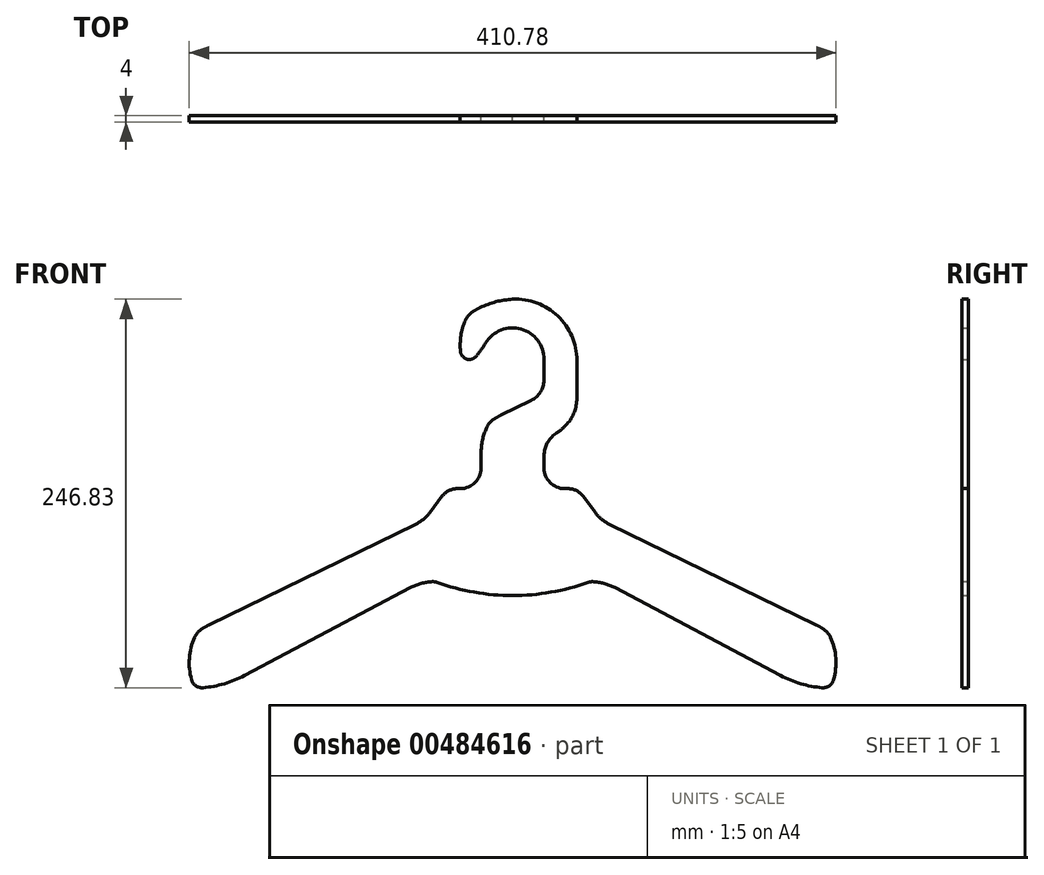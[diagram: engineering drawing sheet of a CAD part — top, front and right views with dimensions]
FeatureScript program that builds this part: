
annotation { "Feature Type Name" : "Feature", "Feature Type Description" : "" }
export const myFeature = defineFeature(function(context is Context, id is Id, definition is map)
    precondition{}
    {
        {
            var Q0;
            Q0=qCreatedBy(makeId("Front.planeOp"),FACE);
            var sketch = newSketch(context, id + "F0", { "sketchPlane" : qUnion([Q0])});
            skLineSegment(sketch, "E0", {"start": v(0, 0) * mm, "end": v(0, 266.9) * mm, "construction": true});
            skLineSegment(sketch, "E1", {"start": v(0, 0) * mm, "end": v(0, -107.96) * mm, "construction": true});
            skSolve(sketch);
        }
        {
            var Q0;
            Q0=qCreatedBy(makeId("Front.planeOp"),FACE);
            var sketch = newSketch(context, id + "F1", { "sketchPlane" : qUnion([Q0])});
            skLineSegment(sketch, "E2", {"start": v(-52.5, 94.84) * mm, "end": v(-44.73, 105.2) * mm});
            skLineSegment(sketch, "E3", {"start": v(-35.13, 110) * mm, "end": v(0, 110) * mm});
            skPoint(sketch, "E4.visualSharp", {"position": v(-56.13, 90) * mm});
            skArc(sketch, "E4.filletArc", {"start": v(-61.56, 87.36) * mm, "mid": v(-56.58, 90.56) * mm, "end": v(-52.5, 94.84) * mm});
            skPoint(sketch, "E5.visualSharp", {"position": v(-41.13, 110) * mm});
            skArc(sketch, "E5.filletArc", {"start": v(-35.13, 110) * mm, "mid": v(-40.5, 108.73) * mm, "end": v(-44.73, 105.2) * mm});
            skLineSegment(sketch, "E6.trimOffspring", {"start": v(-192.69, 23.56) * mm, "end": v(-61.56, 87.36) * mm});
            skLineSegment(sketch, "E7", {"start": v(-309.6, -16.44) * mm, "end": v(-113.2, -16.44) * mm, "construction": true});
            skArc(sketch, "E8", {"start": v(-192.69, 23.56) * mm, "mid": v(-195.08, 22.3) * mm, "end": v(-197.4, 20.87) * mm});
            skArc(sketch, "E9", {"start": v(-197.4, 20.87) * mm, "mid": v(-200.04, 18.5) * mm, "end": v(-201.93, 15.5) * mm});
            skArc(sketch, "E10", {"start": v(-201.93, 15.5) * mm, "mid": v(-205.29, 2.22) * mm, "end": v(-203.88, -11.41) * mm});
            skPoint(sketch, "E11.endSnap0", {"position": v(-198.18, -8.7) * mm});
            skLineSegment(sketch, "E12", {"start": v(-201.8, -34.19) * mm, "end": v(-201.8, 25.75) * mm, "construction": true});
            skArc(sketch, "E13", {"start": v(-203.88, -11.41) * mm, "mid": v(-201.14, -15.23) * mm, "end": v(-196.6, -16.44) * mm});
            skArc(sketch, "E14", {"start": v(-196.6, -16.44) * mm, "mid": v(-183.05, -13.9) * mm, "end": v(-170.27, -8.7) * mm});
            skLineSegment(sketch, "E15", {"start": v(-170.27, -8.7) * mm, "end": v(-64.87, 47.13) * mm});
            skLineSegment(sketch, "E16", {"start": v(-187.28, 42.03) * mm, "end": v(189.28, 42.03) * mm, "construction": true});
            skArc(sketch, "E17", {"start": v(-50.87, 50.92) * mm, "mid": v(-58.08, 49.8) * mm, "end": v(-64.87, 47.13) * mm});
            skArc(sketch, "E18", {"start": v(-50.87, 50.92) * mm, "mid": v(-49.43, 50.84) * mm, "end": v(-48.03, 50.49) * mm});
            skArc(sketch, "E19", {"start": v(-48.03, 50.49) * mm, "mid": v(-24.37, 44.25) * mm, "end": v(0, 42.03) * mm});
            skArc(sketch, "E20.MirrorCS", {"start": v(192.69, 23.56) * mm, "mid": v(195.08, 22.3) * mm, "end": v(197.4, 20.87) * mm});
            skArc(sketch, "E21.MirrorCS", {"start": v(197.4, 20.87) * mm, "mid": v(200.04, 18.5) * mm, "end": v(201.93, 15.5) * mm});
            skArc(sketch, "E22.MirrorCS", {"start": v(61.56, 87.36) * mm, "mid": v(56.58, 90.56) * mm, "end": v(52.5, 94.84) * mm});
            skLineSegment(sketch, "E23.MirrorCS", {"start": v(52.5, 94.84) * mm, "end": v(44.73, 105.2) * mm});
            skArc(sketch, "E24.MirrorCS", {"start": v(50.87, 50.92) * mm, "mid": v(49.43, 50.84) * mm, "end": v(48.03, 50.49) * mm});
            skArc(sketch, "E25.MirrorCS", {"start": v(35.13, 110) * mm, "mid": v(40.5, 108.73) * mm, "end": v(44.73, 105.2) * mm});
            skArc(sketch, "E26.MirrorCS", {"start": v(50.87, 50.92) * mm, "mid": v(58.08, 49.8) * mm, "end": v(64.87, 47.13) * mm});
            skArc(sketch, "E27.MirrorCS", {"start": v(203.88, -11.41) * mm, "mid": v(201.14, -15.23) * mm, "end": v(196.6, -16.44) * mm});
            skArc(sketch, "E28.MirrorCS", {"start": v(201.93, 15.5) * mm, "mid": v(205.29, 2.22) * mm, "end": v(203.88, -11.41) * mm});
            skLineSegment(sketch, "E29.MirrorCS", {"start": v(170.27, -8.7) * mm, "end": v(64.87, 47.13) * mm});
            skPoint(sketch, "E30.MirrorP", {"position": v(41.13, 110) * mm});
            skLineSegment(sketch, "E31.MirrorCS", {"start": v(192.69, 23.56) * mm, "end": v(61.56, 87.36) * mm});
            skLineSegment(sketch, "E32.MirrorCS", {"start": v(35.13, 110) * mm, "end": v(0, 110) * mm});
            skPoint(sketch, "E33.MirrorP", {"position": v(56.13, 90) * mm});
            skPoint(sketch, "E34.MirrorP", {"position": v(198.18, -8.7) * mm});
            skArc(sketch, "E35.MirrorCS", {"start": v(196.6, -16.44) * mm, "mid": v(183.05, -13.9) * mm, "end": v(170.27, -8.7) * mm});
            skArc(sketch, "E36.MirrorCS", {"start": v(48.03, 50.49) * mm, "mid": v(24.37, 44.25) * mm, "end": v(0, 42.03) * mm});
            skSolve(sketch);
        }
        {
            var Q0;
            Q0=qCreatedBy(makeId("Front.planeOp"),FACE);
            var sketch = newSketch(context, id + "F2", { "sketchPlane" : qUnion([Q0])});
            skPoint(sketch, "E37.0", {"position": v(0, 110) * mm});
            skLineSegment(sketch, "E38", {"start": v(244.05, 240) * mm, "end": v(-174.65, 240) * mm, "construction": true});
            skLineSegment(sketch, "E39.0", {"start": v(-35.13, 110) * mm, "end": v(-33, 110) * mm});
            skLineSegment(sketch, "E39.1", {"start": v(35.13, 110) * mm, "end": v(33, 110) * mm});
            skLineSegment(sketch, "E40", {"start": v(20, 123) * mm, "end": v(20, 131) * mm});
            skCircle(sketch, "E41", {"center": v(0, 192.06) * mm, "radius": 20 * mm, "construction": true});
            skLineSegment(sketch, "E42", {"start": v(-7.3, 156.72) * mm, "end": v(11.74, 165.98) * mm});
            skArc(sketch, "E43", {"start": v(-7.3, 156.72) * mm, "mid": v(-9.7, 155.45) * mm, "end": v(-12, 154.03) * mm});
            skArc(sketch, "E44", {"start": v(-12, 154.03) * mm, "mid": v(-14.65, 151.67) * mm, "end": v(-16.55, 148.67) * mm});
            skArc(sketch, "E45", {"start": v(-16.55, 148.67) * mm, "mid": v(-19.13, 140.79) * mm, "end": v(-20, 132.54) * mm});
            skLineSegment(sketch, "E46", {"start": v(-20, 123) * mm, "end": v(-20, 132.54) * mm});
            skArc(sketch, "E47", {"start": v(34.56, 151.04) * mm, "mid": v(31.2, 147.75) * mm, "end": v(27.46, 144.9) * mm});
            skArc(sketch, "E48", {"start": v(27.46, 144.9) * mm, "mid": v(21.98, 138.9) * mm, "end": v(20, 131) * mm});
            skArc(sketch, "E49", {"start": v(11.74, 165.98) * mm, "mid": v(17.63, 171.24) * mm, "end": v(19.88, 178.8) * mm});
            skLineSegment(sketch, "E50", {"start": v(19.88, 178.8) * mm, "end": v(20.05, 192.06) * mm});
            skArc(sketch, "E51", {"start": v(20.05, 192.06) * mm, "mid": v(5.43, 211.36) * mm, "end": v(-17.11, 202.5) * mm});
            skArc(sketch, "E52", {"start": v(-33.1, 197.08) * mm, "mid": v(-29.17, 192.28) * mm, "end": v(-23.22, 194.03) * mm});
            skArc(sketch, "E53", {"start": v(-23.22, 194.03) * mm, "mid": v(-20, 198.15) * mm, "end": v(-17.11, 202.5) * mm});
            skArc(sketch, "E54", {"start": v(-20.7, 225) * mm, "mid": v(-23.09, 223.73) * mm, "end": v(-25.4, 222.31) * mm});
            skArc(sketch, "E55", {"start": v(-25.4, 222.31) * mm, "mid": v(-28.08, 219.91) * mm, "end": v(-29.98, 216.85) * mm});
            skArc(sketch, "E56", {"start": v(-29.98, 216.85) * mm, "mid": v(-32.82, 207.17) * mm, "end": v(-33.1, 197.08) * mm});
            skArc(sketch, "E57", {"start": v(-20.7, 225) * mm, "mid": v(-10.61, 228.7) * mm, "end": v(0, 230.32) * mm});
            skArc(sketch, "E58", {"start": v(0, 230.32) * mm, "mid": v(28.75, 219.65) * mm, "end": v(40.84, 191.46) * mm});
            skLineSegment(sketch, "E59", {"start": v(40.84, 167.38) * mm, "end": v(40.84, 191.46) * mm});
            skArc(sketch, "E60.filletArc", {"start": v(-33, 110) * mm, "mid": v(-23.8, 113.8) * mm, "end": v(-20, 123) * mm});
            skArc(sketch, "E61.filletArc", {"start": v(20, 123) * mm, "mid": v(23.8, 113.8) * mm, "end": v(33, 110) * mm});
            skArc(sketch, "E62", {"start": v(34.56, 151.04) * mm, "mid": v(39.22, 158.63) * mm, "end": v(40.84, 167.38) * mm});
            skLineSegment(sketch, "E63", {"start": v(-33, 110) * mm, "end": v(33, 110) * mm});
            skSolve(sketch);
        }
        {
            var Q0;
            Q0 = qSketchRegion(id + "F1", true);
            extrude(context, id + "F3", {"entities" : qUnion([Q0]), "depth" : 4 * mm, "offsetDistance" : 25 * mm});
        }
        {
            var Q0;
            Q0 = qSketchRegion(id + "F2", true);
            extrude(context, id + "F4", {"entities" : qUnion([Q0]), "operationType" : NewBodyOperationType.ADD, "depth" : 4 * mm, "offsetDistance" : 25 * mm});
        }
    });
